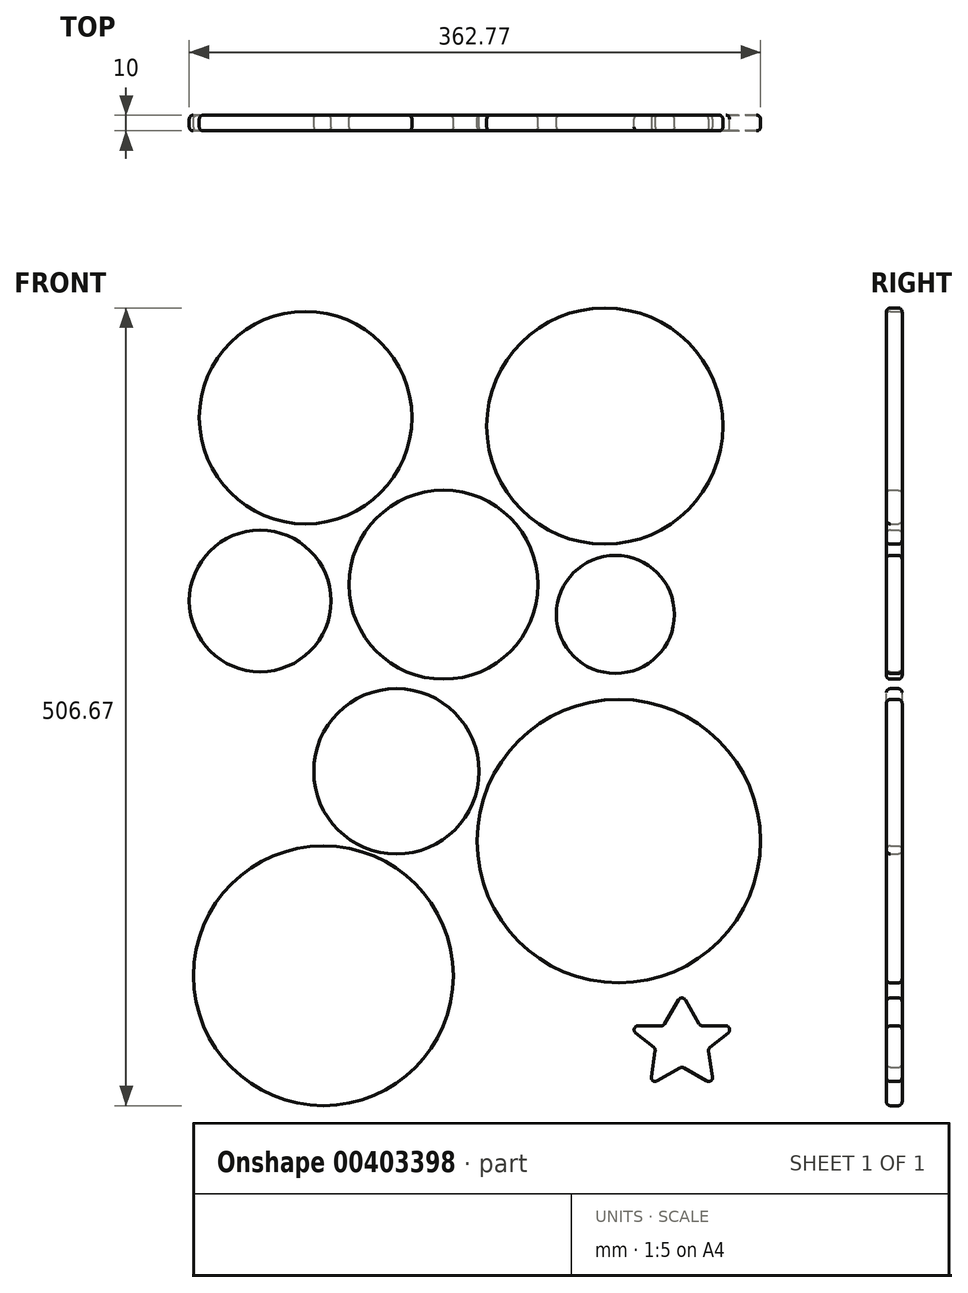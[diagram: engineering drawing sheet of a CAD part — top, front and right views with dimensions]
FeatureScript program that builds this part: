
annotation { "Feature Type Name" : "Feature", "Feature Type Description" : "" }
export const myFeature = defineFeature(function(context is Context, id is Id, definition is map)
    precondition{}
    {
        {
            var Q0;
            Q0=qCreatedBy(makeId("Front.planeOp"),FACE);
            var sketch = newSketch(context, id + "F0", { "sketchPlane" : qUnion([Q0])});
            skLineSegment(sketch, "E0.bottom", {"start": v(172.5, 122.5) * mm, "end": v(-172.5, 122.5) * mm});
            skLineSegment(sketch, "E0.top", {"start": v(172.5, -122.5) * mm, "end": v(-172.5, -122.5) * mm});
            skLineSegment(sketch, "E0.left", {"start": v(172.5, 122.5) * mm, "end": v(172.5, -122.5) * mm});
            skLineSegment(sketch, "E0.right", {"start": v(-172.5, 122.5) * mm, "end": v(-172.5, -122.5) * mm});
            skPoint(sketch, "E0.middle", {"position": v(0, 0) * mm});
            skCircle(sketch, "E1", {"center": v(-95, 47.45) * mm, "radius": 67.5 * mm});
            skLineSegment(sketch, "E2.bottom", {"start": v(-172.5, -122.5) * mm, "end": v(197.5, -122.5) * mm});
            skLineSegment(sketch, "E2.top", {"start": v(-172.5, -392.5) * mm, "end": v(197.5, -392.5) * mm});
            skLineSegment(sketch, "E2.left", {"start": v(-172.5, -122.5) * mm, "end": v(-172.5, -392.5) * mm});
            skLineSegment(sketch, "E2.right", {"start": v(197.5, -122.5) * mm, "end": v(197.5, -392.5) * mm});
            skCircle(sketch, "E3", {"center": v(-83.65, -307.09) * mm, "radius": 82.5 * mm});
            skCircle(sketch, "E4", {"center": v(103.92, -221.55) * mm, "radius": 90 * mm});
            skCircle(sketch, "E5", {"center": v(95.05, 42.08) * mm, "radius": 75 * mm});
            skLineSegment(sketch, "E6", {"start": v(436.8, -80.25) * mm, "end": v(444.07, -80.2) * mm});
            skLineSegment(sketch, "E7", {"start": v(444.07, -80.2) * mm, "end": v(443.95, -60.2) * mm});
            skLineSegment(sketch, "E8", {"start": v(443.95, -60.2) * mm, "end": v(436.8, -80.25) * mm});
            skCircle(sketch, "E9", {"center": v(-7.39, -58.7) * mm, "radius": 60 * mm});
            skCircle(sketch, "E10", {"center": v(-37.28, -177.23) * mm, "radius": 52.5 * mm});
            skCircle(sketch, "E11", {"center": v(-123.85, -69.01) * mm, "radius": 45 * mm});
            skCircle(sketch, "E12", {"center": v(101.76, -77.55) * mm, "radius": 37.5 * mm});
            skLineSegment(sketch, "E13", {"start": v(132.37, -338.89) * mm, "end": v(144.03, -318.68) * mm});
            skLineSegment(sketch, "E14", {"start": v(144.03, -318.68) * mm, "end": v(155.7, -338.89) * mm});
            skLineSegment(sketch, "E15", {"start": v(155.7, -338.89) * mm, "end": v(179.03, -338.89) * mm});
            skLineSegment(sketch, "E16", {"start": v(179.03, -338.89) * mm, "end": v(160.78, -353.42) * mm});
            skLineSegment(sketch, "E17", {"start": v(160.78, -353.42) * mm, "end": v(164.24, -376.5) * mm});
            skLineSegment(sketch, "E18", {"start": v(144.03, -364.83) * mm, "end": v(164.24, -376.5) * mm});
            skLineSegment(sketch, "E19", {"start": v(144.03, -364.83) * mm, "end": v(123.82, -376.5) * mm});
            skLineSegment(sketch, "E20", {"start": v(127.29, -353.42) * mm, "end": v(123.82, -376.5) * mm});
            skLineSegment(sketch, "E21", {"start": v(127.29, -353.42) * mm, "end": v(109.03, -338.89) * mm});
            skLineSegment(sketch, "E22", {"start": v(109.03, -338.89) * mm, "end": v(132.37, -338.89) * mm});
            skLineSegment(sketch, "E23", {"start": v(144.03, -318.68) * mm, "end": v(144.03, -364.83) * mm, "construction": true});
            skLineSegment(sketch, "E24", {"start": v(123.82, -376.5) * mm, "end": v(164.24, -376.5) * mm, "construction": true});
            skPoint(sketch, "E25", {"position": v(144.03, -376.5) * mm});
            skSolve(sketch);
        }
        {
            var Q0;
            Q0=makeQuery(id+"F0.imprint","IMPRINT",FACE,{"disambiguationData":[TD([[makeQuery(id+"F0.imprint","IMPRINT",EDGE,{"derivedFrom":sQuery(id+"F0.wireOp",EDGE,"E1")}),1.0]])]});
            var Q1;
            Q1=makeQuery(id+"F0.imprint","IMPRINT",FACE,{"disambiguationData":[TD([[makeQuery(id+"F0.imprint","IMPRINT",EDGE,{"derivedFrom":sQuery(id+"F0.wireOp",EDGE,"E5")}),1.0]])]});
            var Q2;
            Q2=makeQuery(id+"F0.imprint","IMPRINT",FACE,{"disambiguationData":[TD([[makeQuery(id+"F0.imprint","IMPRINT",EDGE,{"derivedFrom":sQuery(id+"F0.wireOp",EDGE,"E11")}),1.0]])]});
            var Q3;
            Q3=makeQuery(id+"F0.imprint","IMPRINT",FACE,{"disambiguationData":[TD([[makeQuery(id+"F0.imprint","IMPRINT",EDGE,{"derivedFrom":sQuery(id+"F0.wireOp",EDGE,"E9")}),1.0]])]});
            var Q4;
            Q4=makeQuery(id+"F0.imprint","IMPRINT",FACE,{"disambiguationData":[TD([[makeQuery(id+"F0.imprint","IMPRINT",EDGE,{"derivedFrom":sQuery(id+"F0.wireOp",EDGE,"E12")}),1.0]])]});
            var Q5;
            Q5=makeQuery(id+"F0.imprint","IMPRINT",FACE,{"disambiguationData":[TD([[makeQuery(id+"F0.imprint","IMPRINT",EDGE,{"derivedFrom":sQuery(id+"F0.wireOp",EDGE,"E4")}),1.0]])]});
            var Q6;
            Q6=makeQuery(id+"F0.imprint","IMPRINT",FACE,{"disambiguationData":[TD([[makeQuery(id+"F0.imprint","IMPRINT",EDGE,{"derivedFrom":sQuery(id+"F0.wireOp",EDGE,"E10")}),1.0]])]});
            var Q7;
            Q7=makeQuery(id+"F0.imprint","IMPRINT",FACE,{"disambiguationData":[TD([[makeQuery(id+"F0.imprint","IMPRINT",EDGE,{"derivedFrom":sQuery(id+"F0.wireOp",EDGE,"E3")}),1.0]])]});
            var Q8;
            Q8=makeQuery(id+"F0.imprint","IMPRINT",FACE,{"disambiguationData":[TD([[makeQuery(id+"F0.imprint","IMPRINT",EDGE,{"derivedFrom":sQuery(id+"F0.wireOp",EDGE,"E13")}),-1.0]])]});
            extrude(context, id + "F1", {"entities" : qUnion([Q0, Q1, Q2, Q3, Q4, Q5, Q6, Q7, Q8]), "endBound" : BoundingType.SYMMETRIC, "depth" : 10 * mm, "hasSecondDirection" : true, "secondDirectionOppositeDirection" : true, "secondDirectionDepth" : 25 * mm});
        }
        {
            var Q0;
            Q0=makeQuery(id+"F1.opExtrude","CAP_FACE",FACE,{"disambiguationData":[OSD([sQuery(id+"F0.wireOp",EDGE,"E3")])],"isStart":false});
            var Q1;
            Q1=makeQuery(id+"F1.opExtrude","CAP_FACE",FACE,{"disambiguationData":[OSD([sQuery(id+"F0.wireOp",EDGE,"E4")])],"isStart":false});
            var Q2;
            Q2=makeQuery(id+"F1.opExtrude","CAP_FACE",FACE,{"disambiguationData":[OSD([sQuery(id+"F0.wireOp",EDGE,"E10")])],"isStart":false});
            var Q3;
            Q3=makeQuery(id+"F1.opExtrude","CAP_FACE",FACE,{"disambiguationData":[OSD([sQuery(id+"F0.wireOp",EDGE,"E9")])],"isStart":false});
            var Q4;
            Q4=makeQuery(id+"F1.opExtrude","CAP_FACE",FACE,{"disambiguationData":[OSD([sQuery(id+"F0.wireOp",EDGE,"E12")])],"isStart":false});
            var Q5;
            Q5=makeQuery(id+"F1.opExtrude","CAP_FACE",FACE,{"disambiguationData":[OSD([sQuery(id+"F0.wireOp",EDGE,"E5")])],"isStart":false});
            var Q6;
            Q6=makeQuery(id+"F1.opExtrude","CAP_FACE",FACE,{"disambiguationData":[OSD([sQuery(id+"F0.wireOp",EDGE,"E1")])],"isStart":false});
            var Q7;
            Q7=makeQuery(id+"F1.opExtrude","CAP_FACE",FACE,{"disambiguationData":[OSD([sQuery(id+"F0.wireOp",EDGE,"E11")])],"isStart":false});
            var Q8;
            Q8=makeQuery(id+"F1.opExtrude","CAP_FACE",FACE,{"disambiguationData":[OSD([sQuery(id+"F0.wireOp",EDGE,"E3")])],"isStart":true});
            var Q9;
            Q9=makeQuery(id+"F1.opExtrude","CAP_FACE",FACE,{"disambiguationData":[OSD([sQuery(id+"F0.wireOp",EDGE,"E4")])],"isStart":true});
            var Q10;
            Q10=makeQuery(id+"F1.opExtrude","CAP_FACE",FACE,{"disambiguationData":[OSD([sQuery(id+"F0.wireOp",EDGE,"E10")])],"isStart":true});
            var Q11;
            Q11=makeQuery(id+"F1.opExtrude","CAP_FACE",FACE,{"disambiguationData":[OSD([sQuery(id+"F0.wireOp",EDGE,"E11")])],"isStart":true});
            var Q12;
            Q12=makeQuery(id+"F1.opExtrude","CAP_FACE",FACE,{"disambiguationData":[OSD([sQuery(id+"F0.wireOp",EDGE,"E9")])],"isStart":true});
            var Q13;
            Q13=makeQuery(id+"F1.opExtrude","CAP_FACE",FACE,{"disambiguationData":[OSD([sQuery(id+"F0.wireOp",EDGE,"E12")])],"isStart":true});
            var Q14;
            Q14=makeQuery(id+"F1.opExtrude","CAP_FACE",FACE,{"disambiguationData":[OSD([sQuery(id+"F0.wireOp",EDGE,"E5")])],"isStart":true});
            var Q15;
            Q15=makeQuery(id+"F1.opExtrude","CAP_FACE",FACE,{"disambiguationData":[OSD([sQuery(id+"F0.wireOp",EDGE,"E1")])],"isStart":true});
            var Q16;
            Q16=makeQuery(id+"F1.opExtrude","CAP_FACE",FACE,{"disambiguationData":[OSD([sQuery(id+"F0.wireOp",EDGE,"E13"),sQuery(id+"F0.wireOp",EDGE,"E14"),sQuery(id+"F0.wireOp",EDGE,"E15"),sQuery(id+"F0.wireOp",EDGE,"E16"),sQuery(id+"F0.wireOp",EDGE,"E17"),sQuery(id+"F0.wireOp",EDGE,"E18"),sQuery(id+"F0.wireOp",EDGE,"E19"),sQuery(id+"F0.wireOp",EDGE,"E20"),sQuery(id+"F0.wireOp",EDGE,"E21"),sQuery(id+"F0.wireOp",EDGE,"E22")])],"isStart":false});
            var Q17;
            Q17=makeQuery(id+"F1.opExtrude","SWEPT_FACE",FACE,{"disambiguationData":[OSD([sQuery(id+"F0.wireOp",EDGE,"E18")])]});
            var Q18;
            Q18=makeQuery(id+"F1.opExtrude","SWEPT_FACE",FACE,{"disambiguationData":[OSD([sQuery(id+"F0.wireOp",EDGE,"E19")])]});
            var Q19;
            Q19=makeQuery(id+"F1.opExtrude","SWEPT_FACE",FACE,{"disambiguationData":[OSD([sQuery(id+"F0.wireOp",EDGE,"E16")])]});
            var Q20;
            Q20=makeQuery(id+"F1.opExtrude","SWEPT_FACE",FACE,{"disambiguationData":[OSD([sQuery(id+"F0.wireOp",EDGE,"E17")])]});
            var Q21;
            Q21=makeQuery(id+"F1.opExtrude","SWEPT_FACE",FACE,{"disambiguationData":[OSD([sQuery(id+"F0.wireOp",EDGE,"E15")])]});
            var Q22;
            Q22=makeQuery(id+"F1.opExtrude","SWEPT_FACE",FACE,{"disambiguationData":[OSD([sQuery(id+"F0.wireOp",EDGE,"E14")])]});
            var Q23;
            Q23=makeQuery(id+"F1.opExtrude","SWEPT_FACE",FACE,{"disambiguationData":[OSD([sQuery(id+"F0.wireOp",EDGE,"E13")])]});
            var Q24;
            Q24=makeQuery(id+"F1.opExtrude","SWEPT_FACE",FACE,{"disambiguationData":[OSD([sQuery(id+"F0.wireOp",EDGE,"E22")])]});
            var Q25;
            Q25=makeQuery(id+"F1.opExtrude","SWEPT_FACE",FACE,{"disambiguationData":[OSD([sQuery(id+"F0.wireOp",EDGE,"E21")])]});
            var Q26;
            Q26=makeQuery(id+"F1.opExtrude","SWEPT_FACE",FACE,{"disambiguationData":[OSD([sQuery(id+"F0.wireOp",EDGE,"E20")])]});
            fillet(context, id + "F2", {"entities" : qUnion([Q0, Q1, Q2, Q3, Q4, Q5, Q6, Q7, Q8, Q9, Q10, Q11, Q12, Q13, Q14, Q15, Q16, Q17, Q18, Q19, Q20, Q21, Q22, Q23, Q24, Q25, Q26]), "radius" : 2.5 * mm, "tangentPropagation" : true, "allowEdgeOverflow" : false});
        }
    });
